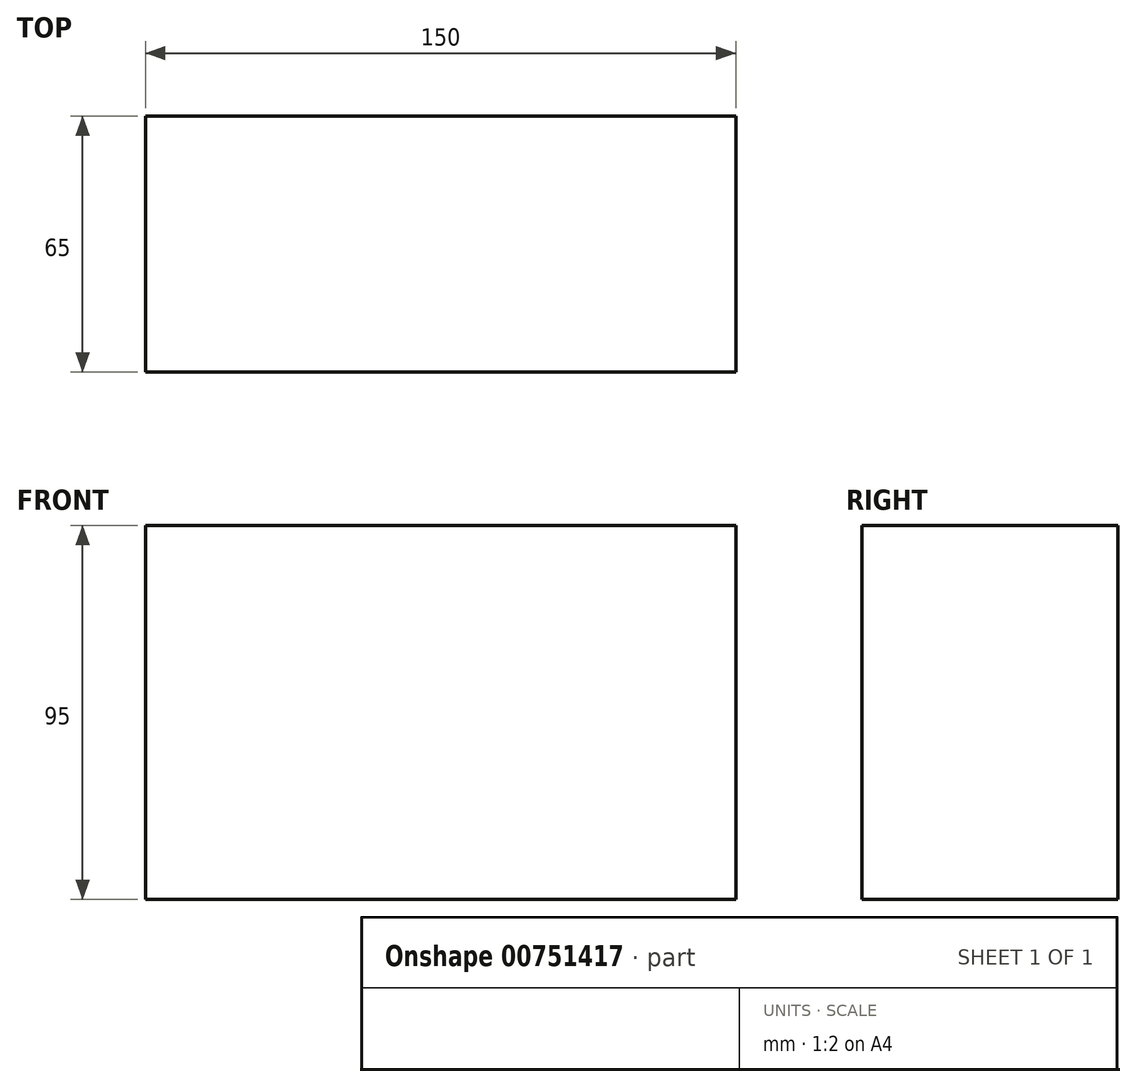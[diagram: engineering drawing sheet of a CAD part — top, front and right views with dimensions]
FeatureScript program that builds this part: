
annotation { "Feature Type Name" : "Feature", "Feature Type Description" : "" }
export const myFeature = defineFeature(function(context is Context, id is Id, definition is map)
    precondition{}
    {
        {
            var Q0;
            Q0=qCreatedBy(makeId("Top.planeOp"),FACE);
            var sketch = newSketch(context, id + "F0", { "sketchPlane" : qUnion([Q0])});
            skLineSegment(sketch, "E0.bottom", {"start": v(-59.12, 36.55) * mm, "end": v(90.88, 36.55) * mm});
            skLineSegment(sketch, "E0.top", {"start": v(-59.12, -28.45) * mm, "end": v(90.88, -28.45) * mm});
            skLineSegment(sketch, "E0.left", {"start": v(-59.12, 36.55) * mm, "end": v(-59.12, -28.45) * mm});
            skLineSegment(sketch, "E0.right", {"start": v(90.88, 36.55) * mm, "end": v(90.88, -28.45) * mm});
            skSolve(sketch);
        }
        {
            var Q0;
            Q0=makeQuery(id+"F0.imprint","IMPRINT",FACE,{"disambiguationData":[TD([[makeQuery(id+"F0.imprint","IMPRINT",EDGE,{"derivedFrom":sQuery(id+"F0.wireOp",EDGE,"E0.bottom")}),-1.0]])]});
            extrude(context, id + "F1", {"entities" : qUnion([Q0]), "depth" : 95 * mm, "offsetDistance" : 25.4 * mm});
        }
    });
